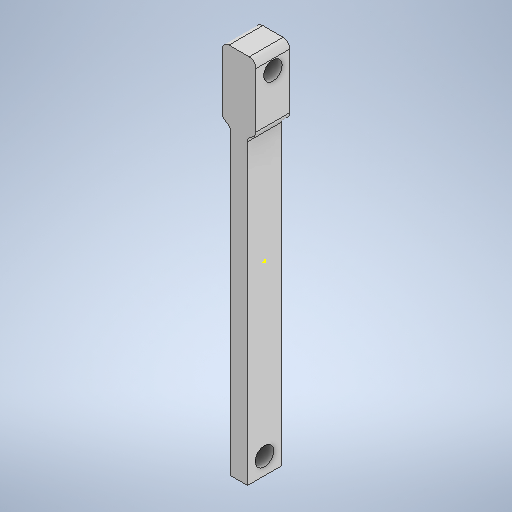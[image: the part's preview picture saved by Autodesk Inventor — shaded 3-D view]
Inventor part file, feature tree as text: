
AUTODESK INVENTOR PART (.ipt)
format: ipt  version: 2025.2 (Build 292293000, 293)  size: 279,040 bytes
history: native  units: mm
features: sketch x5, extrude x4, other x1, fillet x1
ambient origin geometry x8: Origin, YZ Plane, XZ Plane, XY Plane, X Axis, Y Axis, Z Axis, Center Point
bodies: Body1 (feature_tree)
feature tree (11):
  other  "Bryła1"
  extrude  "Wyciągnięcie proste1"  Depth=5.0mm
  extrude  "Wyciągnięcie proste3"  Depth=10.0mm
  sketch  "Szkic4"
  extrude  "Wyciągnięcie proste4"  Depth=110.0mm TaperAngle=0.0deg
  extrude  "Wyciągnięcie proste5"  Depth=5.5mm
  fillet  "Zaokrąglenie3"  Radius=5.0mm
  sketch  "Szkic1"
  sketch  "Szkic3"
  sketch  "Szkic5"
  sketch  "Szkic6"
